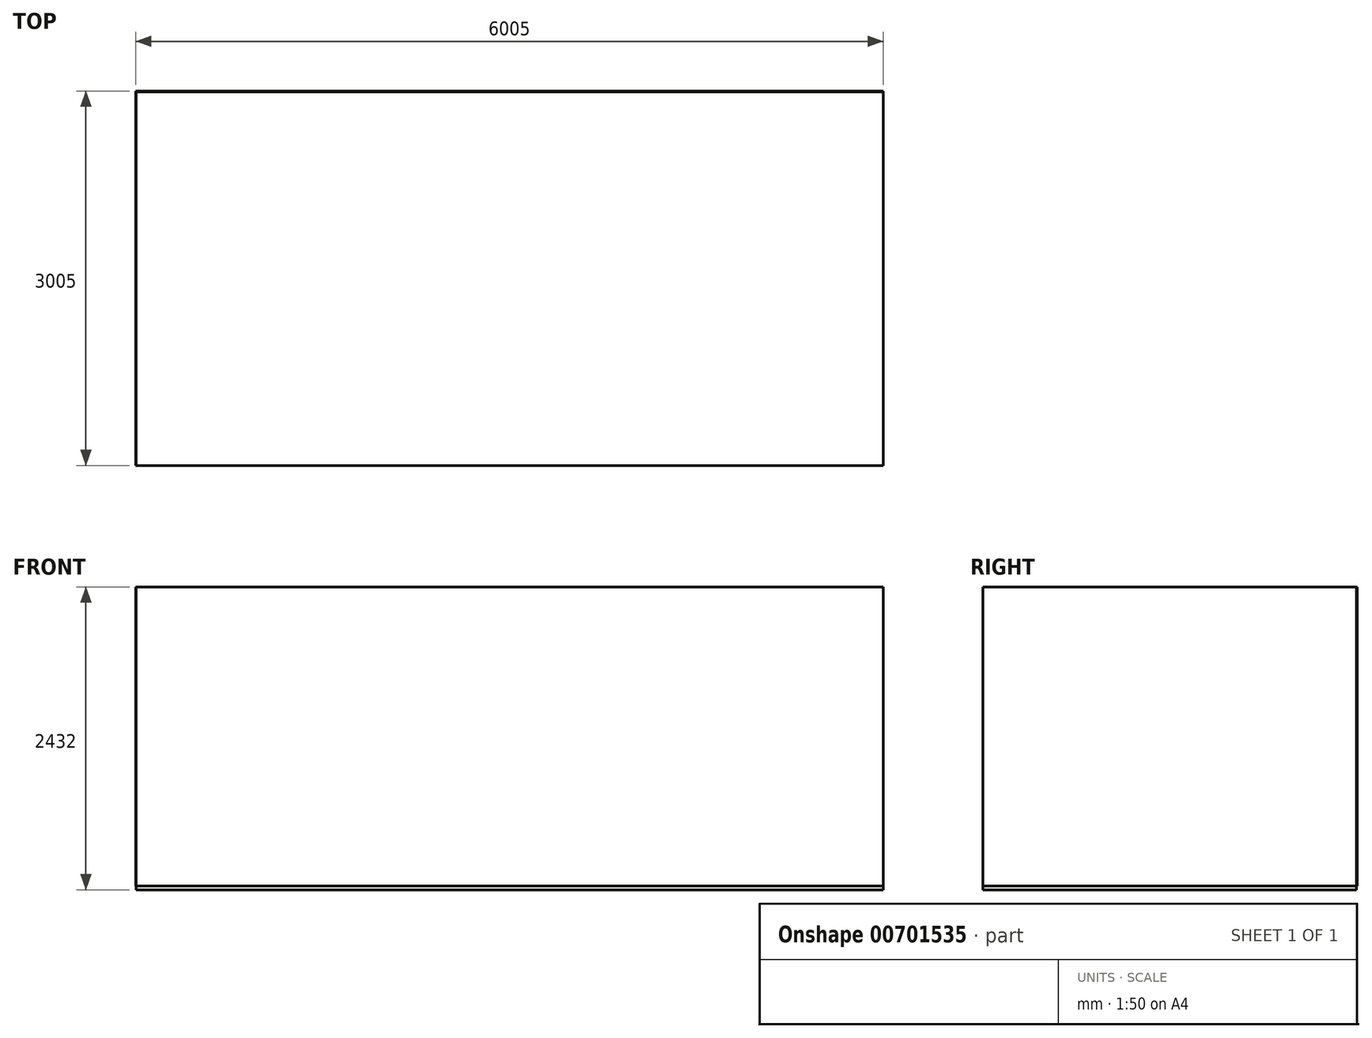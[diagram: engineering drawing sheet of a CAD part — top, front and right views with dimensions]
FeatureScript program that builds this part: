
annotation { "Feature Type Name" : "Feature", "Feature Type Description" : "" }
export const myFeature = defineFeature(function(context is Context, id is Id, definition is map)
    precondition{}
    {
        {
            var Q0;
            Q0=qCreatedBy(makeId("Top.planeOp"),FACE);
            var sketch = newSketch(context, id + "F0", { "sketchPlane" : qUnion([Q0]), "disableImprinting" : false});
            skLineSegment(sketch, "E0.bottom", {"start": v(3000, 1500) * mm, "end": v(-3000, 1500) * mm});
            skLineSegment(sketch, "E0.top", {"start": v(3000, -1500) * mm, "end": v(-3000, -1500) * mm});
            skLineSegment(sketch, "E0.left", {"start": v(3000, 1500) * mm, "end": v(3000, -1500) * mm});
            skLineSegment(sketch, "E0.right", {"start": v(-3000, 1500) * mm, "end": v(-3000, -1500) * mm});
            skPoint(sketch, "E0.middle", {"position": v(0, 0) * mm});
            skSolve(sketch);
        }
        {
            var Q0;
            Q0=makeQuery(id+"F0.imprint","IMPRINT",FACE,{"disambiguationData":[TD([[makeQuery(id+"F0.imprint","IMPRINT",EDGE,{"derivedFrom":sQuery(id+"F0.wireOp",EDGE,"E0.bottom")}),1.0]])]});
            var sketch = newSketch(context, id + "F1", { "sketchPlane" : qUnion([Q0])});
            skSolve(sketch);
        }
        {
            var Q0;
            Q0 = qSketchRegion(id + "F1", true);
            var Q1;
            Q1=makeQuery(id+"F0.imprint","IMPRINT",FACE,{"disambiguationData":[TD([[makeQuery(id+"F0.imprint","IMPRINT",EDGE,{"derivedFrom":sQuery(id+"F0.wireOp",EDGE,"E0.bottom")}),1.0]])]});
            extrude(context, id + "F2", {"entities" : qUnion([Q0, Q1]), "oppositeDirection" : true, "depth" : 32 * mm, "offsetDistance" : 25 * mm});
        }
        {
            var Q0;
            Q0=qCreatedBy(makeId("Top.planeOp"),FACE);
            var sketch = newSketch(context, id + "F3", { "sketchPlane" : qUnion([Q0]), "disableImprinting" : false});
            skLineSegment(sketch, "E1.bottom", {"start": v(-3000, 1500) * mm, "end": v(3000, 1500) * mm});
            skPoint(sketch, "E1.middle", {"position": v(0, 0) * mm});
            skLineSegment(sketch, "E2.0", {"start": v(-3005, 1505) * mm, "end": v(3000, 1505) * mm});
            skLineSegment(sketch, "E3", {"start": v(-3005, -1500) * mm, "end": v(-3000, -1500) * mm});
            skLineSegment(sketch, "E4", {"start": v(3000, 1505) * mm, "end": v(3000, 1500) * mm});
            skLineSegment(sketch, "E5", {"start": v(-3005, 1505) * mm, "end": v(-3005, -1500) * mm});
            skLineSegment(sketch, "E6", {"start": v(-3000, 1500) * mm, "end": v(-3000, -1500) * mm});
            skSolve(sketch);
        }
        {
            var Q0;
            Q0=makeQuery(id+"F3.imprint","IMPRINT",FACE,{"disambiguationData":[TD([[makeQuery(id+"F3.imprint","IMPRINT",EDGE,{"derivedFrom":sQuery(id+"F3.wireOp",EDGE,"E1.bottom")}),1.0]])]});
            extrude(context, id + "F4", {"entities" : qUnion([Q0]), "flatOperationType" : FlatOperationType.REMOVE, "depth" : 2400 * mm, "offsetDistance" : 25 * mm, "domain" : OperationDomain.MODEL});
        }
    });
